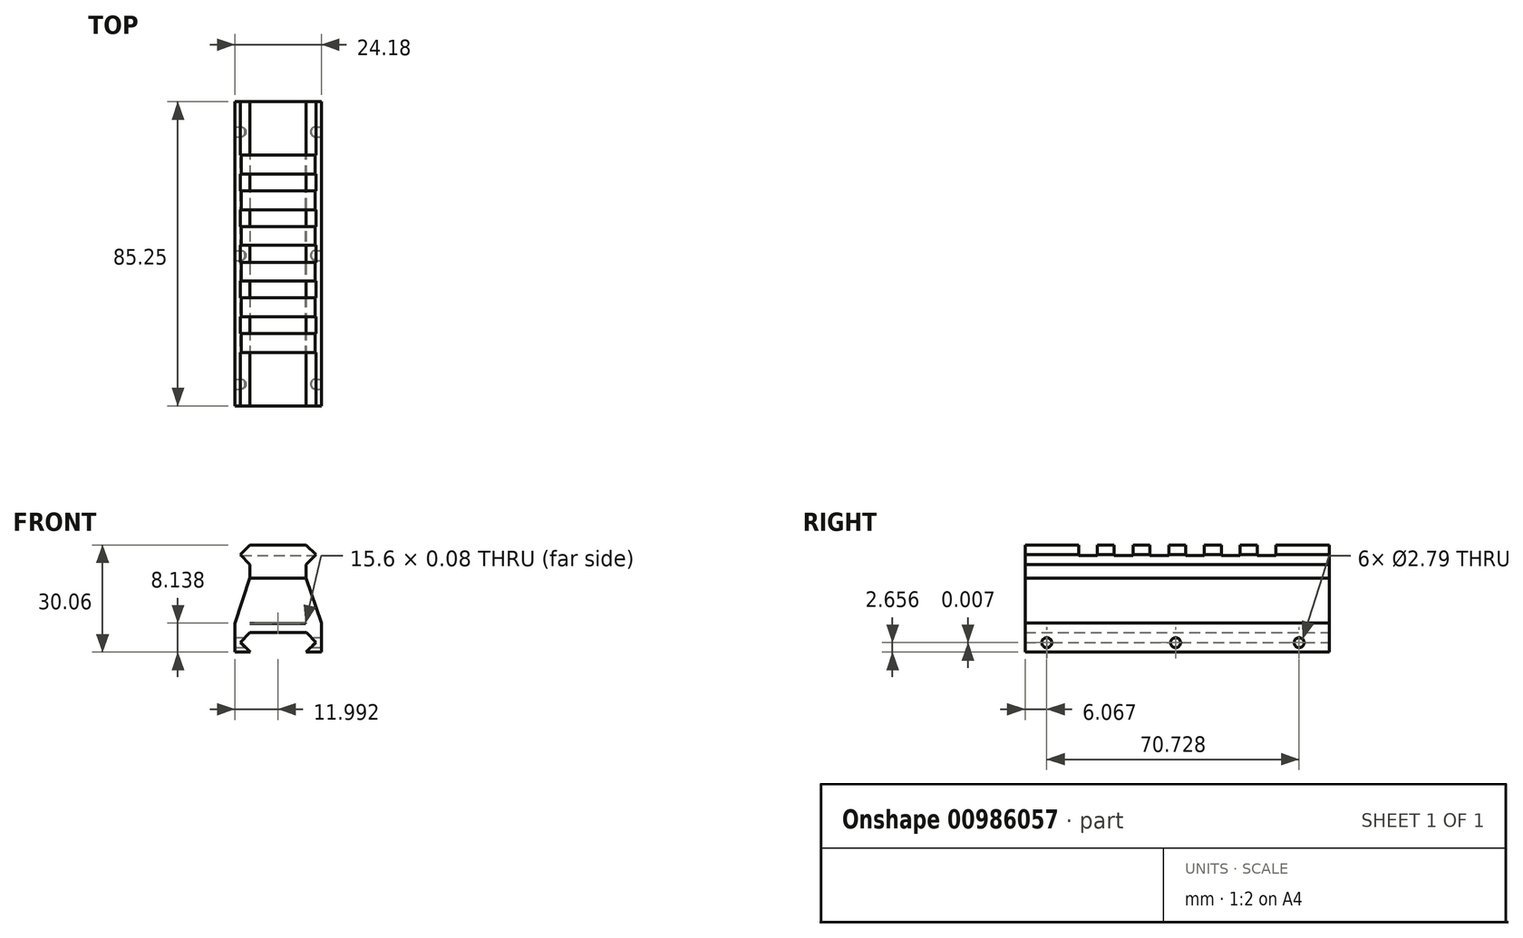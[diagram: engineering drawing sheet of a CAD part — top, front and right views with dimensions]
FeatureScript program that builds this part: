
annotation { "Feature Type Name" : "Feature", "Feature Type Description" : "" }
export const myFeature = defineFeature(function(context is Context, id is Id, definition is map)
    precondition{}
    {
        {
            var Q0;
            Q0=qCreatedBy(makeId("Front.planeOp"),FACE);
            var sketch = newSketch(context, id + "F0", { "sketchPlane" : qUnion([Q0])});
            skLineSegment(sketch, "E0", {"start": v(0, 0) * mm, "end": v(15.67, 0) * mm});
            skPoint(sketch, "E1", {"position": v(0, 9.32) * mm});
            skLineSegment(sketch, "E2", {"start": v(0, 9.32) * mm, "end": v(-2.77, 6.55) * mm});
            skLineSegment(sketch, "E3", {"start": v(0, 9.32) * mm, "end": v(15.67, 9.32) * mm});
            skLineSegment(sketch, "E4", {"start": v(-2.77, 6.56) * mm, "end": v(0, 3.8) * mm});
            skLineSegment(sketch, "E5", {"start": v(0, 3.8) * mm, "end": v(0, 0) * mm});
            skLineSegment(sketch, "E6", {"start": v(15.67, 9.32) * mm, "end": v(18.43, 6.56) * mm});
            skLineSegment(sketch, "E7", {"start": v(18.43, 6.56) * mm, "end": v(15.67, 3.8) * mm});
            skLineSegment(sketch, "E8", {"start": v(15.67, 3.8) * mm, "end": v(15.67, 0) * mm});
            skSolve(sketch);
        }
        {
            var Q0;
            Q0=makeQuery(id+"F0.imprint","IMPRINT",FACE,{"disambiguationData":[TD([[makeQuery(id+"F0.imprint","IMPRINT",EDGE,{"derivedFrom":sQuery(id+"F0.wireOp",EDGE,"E0")}),1.0]])]});
            extrude(context, id + "F1", {"entities" : qUnion([Q0]), "depth" : 85.25 * mm, "offsetDistance" : 25 * mm});
        }
        {
            var Q0;
            Q0=makeQuery(id+"F1.opExtrude","SWEPT_FACE",FACE,{"disambiguationData":[OSD([sQuery(id+"F0.wireOp",EDGE,"E3")])]});
            var sketch = newSketch(context, id + "F2", { "sketchPlane" : qUnion([Q0])});
            skLineSegment(sketch, "E9", {"start": v(-19.7, -15) * mm, "end": v(36.12, -15) * mm});
            skLineSegment(sketch, "E10", {"start": v(-19.7, -20.25) * mm, "end": v(36.12, -20.25) * mm});
            skLineSegment(sketch, "E11", {"start": v(-19.7, -15) * mm, "end": v(-19.7, -20.25) * mm});
            skLineSegment(sketch, "E12", {"start": v(36.12, -15) * mm, "end": v(36.12, -20.25) * mm});
            skPoint(sketch, "E13", {"position": v(-19.7, -25) * mm});
            skLineSegment(sketch, "E14.0.1.0", {"start": v(-19.7, -25) * mm, "end": v(36.12, -25) * mm});
            skLineSegment(sketch, "E14.0.1.1", {"start": v(-19.7, -25) * mm, "end": v(-19.7, -30.25) * mm});
            skPoint(sketch, "E14.0.1.2", {"position": v(-19.7, -35) * mm});
            skLineSegment(sketch, "E14.0.1.3", {"start": v(-19.7, -30.25) * mm, "end": v(36.12, -30.25) * mm});
            skLineSegment(sketch, "E14.0.1.4", {"start": v(36.12, -25) * mm, "end": v(36.12, -30.25) * mm});
            skLineSegment(sketch, "E14.0.2.0", {"start": v(-19.7, -35) * mm, "end": v(36.12, -35) * mm});
            skLineSegment(sketch, "E14.0.2.1", {"start": v(-19.7, -35) * mm, "end": v(-19.7, -40.25) * mm});
            skPoint(sketch, "E14.0.2.2", {"position": v(-19.7, -45) * mm});
            skLineSegment(sketch, "E14.0.2.3", {"start": v(-19.7, -40.25) * mm, "end": v(36.12, -40.25) * mm});
            skLineSegment(sketch, "E14.0.2.4", {"start": v(36.12, -35) * mm, "end": v(36.12, -40.25) * mm});
            skLineSegment(sketch, "E14.0.3.0", {"start": v(-19.7, -45) * mm, "end": v(36.12, -45) * mm});
            skLineSegment(sketch, "E14.0.3.1", {"start": v(-19.7, -45) * mm, "end": v(-19.7, -50.25) * mm});
            skPoint(sketch, "E14.0.3.2", {"position": v(-19.7, -55) * mm});
            skLineSegment(sketch, "E14.0.3.3", {"start": v(-19.7, -50.25) * mm, "end": v(36.12, -50.25) * mm});
            skLineSegment(sketch, "E14.0.3.4", {"start": v(36.12, -45) * mm, "end": v(36.12, -50.25) * mm});
            skLineSegment(sketch, "E14.0.4.0", {"start": v(-19.7, -55) * mm, "end": v(36.12, -55) * mm});
            skLineSegment(sketch, "E14.0.4.1", {"start": v(-19.7, -55) * mm, "end": v(-19.7, -60.25) * mm});
            skPoint(sketch, "E14.0.4.2", {"position": v(-19.7, -65) * mm});
            skLineSegment(sketch, "E14.0.4.3", {"start": v(-19.7, -60.25) * mm, "end": v(36.12, -60.25) * mm});
            skLineSegment(sketch, "E14.0.4.4", {"start": v(36.12, -55) * mm, "end": v(36.12, -60.25) * mm});
            skLineSegment(sketch, "E14.0.5.0", {"start": v(-19.7, -65) * mm, "end": v(36.12, -65) * mm});
            skLineSegment(sketch, "E14.0.5.1", {"start": v(-19.7, -65) * mm, "end": v(-19.7, -70.25) * mm});
            skPoint(sketch, "E14.0.5.2", {"position": v(-19.7, -75) * mm});
            skLineSegment(sketch, "E14.0.5.3", {"start": v(-19.7, -70.25) * mm, "end": v(36.12, -70.25) * mm});
            skLineSegment(sketch, "E14.0.5.4", {"start": v(36.12, -65) * mm, "end": v(36.12, -70.25) * mm});
            skLineSegment(sketch, "E14.direction1", {"start": v(-19.7, -15) * mm, "end": v(12.9, -15) * mm, "construction": true});
            skLineSegment(sketch, "E14.direction2", {"start": v(-19.7, -15) * mm, "end": v(-19.7, -25) * mm, "construction": true});
            skSolve(sketch);
        }
        {
            var Q0;
            Q0=qSketchRegion(id+"F2",true);
            extrude(context, id + "F3", {"entities" : qUnion([Q0]), "operationType" : NewBodyOperationType.REMOVE, "oppositeDirection" : true, "depth" : 3 * mm, "offsetDistance" : 25 * mm});
        }
        {
            var Q0;
            Q0=qCreatedBy(makeId("Front.planeOp"),FACE);
            var sketch = newSketch(context, id + "F4", { "sketchPlane" : qUnion([Q0])});
            skLineSegment(sketch, "E15.top", {"start": v(0, -2.55) * mm, "end": v(0, -2.55) * mm});
            skLineSegment(sketch, "E16", {"start": v(15.68, -20.74) * mm, "end": v(18.45, -17.97) * mm});
            skLineSegment(sketch, "E17", {"start": v(18.45, -17.97) * mm, "end": v(15.68, -15.21) * mm});
            skLineSegment(sketch, "E18.MirrorCS", {"start": v(-2.69, -17.97) * mm, "end": v(0.09, -15.2) * mm});
            skLineSegment(sketch, "E19.MirrorCS", {"start": v(0.08, -20.74) * mm, "end": v(-2.69, -17.97) * mm});
            skLineSegment(sketch, "E20.bottom", {"start": v(0.08, -20.74) * mm, "end": v(-4.19, -20.74) * mm});
            skLineSegment(sketch, "E21.top", {"start": v(15.76, -15.3) * mm, "end": v(0, -15.3) * mm});
            skLineSegment(sketch, "E22.right", {"start": v(-4.19, -12.66) * mm, "end": v(-4.19, -20.74) * mm});
            skLineSegment(sketch, "E23.top", {"start": v(20, -20.74) * mm, "end": v(15.68, -20.74) * mm});
            skLineSegment(sketch, "E23.left", {"start": v(20, -12.54) * mm, "end": v(20, -20.74) * mm});
            skLineSegment(sketch, "E23.right", {"start": v(15.6, 0.12) * mm, "end": v(15.6, 0) * mm});
            skLineSegment(sketch, "E24", {"start": v(20, -12.54) * mm, "end": v(-4.19, -12.66) * mm});
            skLineSegment(sketch, "E25.bottom", {"start": v(15.6, 0.12) * mm, "end": v(0, 0.12) * mm});
            skLineSegment(sketch, "E25.top", {"start": v(15.6, -12.64) * mm, "end": v(0, -12.64) * mm});
            skLineSegment(sketch, "E25.left", {"start": v(15.6, 0.12) * mm, "end": v(15.6, -12.64) * mm});
            skLineSegment(sketch, "E25.right", {"start": v(0, 0.12) * mm, "end": v(0, -12.64) * mm});
            skLineSegment(sketch, "E26", {"start": v(15.6, 0.12) * mm, "end": v(20, -12.54) * mm});
            skLineSegment(sketch, "E27", {"start": v(0, 0.12) * mm, "end": v(-4.19, -12.66) * mm});
            skSolve(sketch);
        }
        {
            var Q0;
            {var subQ2=sQuery(id+"F4.wireOp",EDGE,"E23.right");Q0=makeQuery(id+"F4.imprint","IMPRINT",FACE,{"disambiguationData":[TD([[makeQuery(id+"F4.imprint","IMPRINT",EDGE,{"derivedFrom":subQ2}),-1.0]])]});}
            var Q1;
            {var subQ6=sQuery(id+"F4.wireOp",EDGE,"E16");Q1=makeQuery(id+"F4.imprint","IMPRINT",FACE,{"disambiguationData":[TD([[makeQuery(id+"F4.imprint","IMPRINT",EDGE,{"derivedFrom":subQ6}),-1.0]])]});}
            var Q2;
            {var subQ0=sQuery(id+"F4.wireOp",EDGE,"E23.right");Q2=makeQuery(id+"F4.imprint","IMPRINT",FACE,{"disambiguationData":[TD([[makeQuery(id+"F4.imprint","IMPRINT",EDGE,{"derivedFrom":subQ0}),1.0]])]});}
            var Q3;
            {var subQ0=sQuery(id+"F4.wireOp",EDGE,"E27");Q3=makeQuery(id+"F4.imprint","IMPRINT",FACE,{"disambiguationData":[TD([[makeQuery(id+"F4.imprint","IMPRINT",EDGE,{"derivedFrom":subQ0}),1.0]])]});}
            extrude(context, id + "F5", {"entities" : qUnion([Q0, Q1, Q2, Q3]), "operationType" : NewBodyOperationType.ADD, "depth" : 85.24 * mm, "offsetDistance" : 25.4 * mm});
        }
        {
            var Q0;
            Q0=qCreatedBy(makeId("Right.planeOp"),FACE);
            var sketch = newSketch(context, id + "F6", { "sketchPlane" : qUnion([Q0])});
            skPoint(sketch, "E28", {"position": v(-8.46, -18.08) * mm});
            skPoint(sketch, "E29", {"position": v(-79.18, -18.08) * mm});
            skPoint(sketch, "E30", {"position": v(-43.07, -18.08) * mm});
            skSolve(sketch);
        }
        {
            var Q0;
            Q0=makeQuery(id+"F5.opExtrude","SWEPT_FACE",FACE,{"disambiguationData":[OSD([sQuery(id+"F4.wireOp",EDGE,"E23.left")])]});
            var sketch = newSketch(context, id + "F7", { "sketchPlane" : qUnion([Q0])});
            skPoint(sketch, "E31", {"position": v(-79.18, -18.08) * mm});
            skPoint(sketch, "E32", {"position": v(-43.08, -18.08) * mm});
            skPoint(sketch, "E33", {"position": v(-8.45, -18.08) * mm});
            skSolve(sketch);
        }
        {
            var Q0;
            Q0=sQuery(id+"F6.wireOp",VERTEX,"E29");
            var Q1;
            Q1=sQuery(id+"F6.wireOp",VERTEX,"E30");
            var Q2;
            Q2=sQuery(id+"F6.wireOp",VERTEX,"E28");
            var Q3;
            Q3=sQuery(id+"F7.wireOp",VERTEX,"E31");
            var Q4;
            Q4=sQuery(id+"F7.wireOp",VERTEX,"E32");
            var Q5;
            Q5=sQuery(id+"F7.wireOp",VERTEX,"E33");
            var Q6;
            Q6=makeQuery(id+"F5.opExtrude","SWEPT_BODY",BODY,{"disambiguationData":[OSD([sQuery(id+"F4.wireOp",EDGE,"E16"),sQuery(id+"F4.wireOp",EDGE,"E17"),sQuery(id+"F4.wireOp",EDGE,"E18.MirrorCS"),sQuery(id+"F4.wireOp",EDGE,"E19.MirrorCS"),sQuery(id+"F4.wireOp",EDGE,"E20.bottom"),sQuery(id+"F4.wireOp",EDGE,"E21.top"),sQuery(id+"F4.wireOp",EDGE,"E22.right"),sQuery(id+"F4.wireOp",EDGE,"E23.top"),sQuery(id+"F4.wireOp",EDGE,"E23.left"),sQuery(id+"F4.wireOp",EDGE,"E24"),sQuery(id+"F4.wireOp",EDGE,"E25.top"),sQuery(id+"F4.wireOp",EDGE,"E25.left"),sQuery(id+"F4.wireOp",EDGE,"E25.right")])]});
            var Q7;
            Q7=makeQuery(id+"F1.opExtrude","SWEPT_BODY",BODY,{"disambiguationData":[OSD([sQuery(id+"F0.wireOp",EDGE,"E0"),sQuery(id+"F0.wireOp",EDGE,"E2"),sQuery(id+"F0.wireOp",EDGE,"E3"),sQuery(id+"F0.wireOp",EDGE,"E4"),sQuery(id+"F0.wireOp",EDGE,"E5"),sQuery(id+"F0.wireOp",EDGE,"E6"),sQuery(id+"F0.wireOp",EDGE,"E7"),sQuery(id+"F0.wireOp",EDGE,"E8")])]});
            hole(context, id + "F8", {"style" : HoleStyle.SIMPLE, "endStyle" : HoleEndStyle.BLIND, "holeDiameter" : 2.8 * mm, "majorDiameter" : 6.35 * mm, "holeDepth" : 12.7 * mm, "isTappedThrough" : true, "tappedDepth" : 12.7 * mm, "tapClearance" : 3, "locations" : qUnion([Q0, Q1, Q2, Q3, Q4, Q5]), "scope" : qUnion([Q6, Q7])});
        }
    });
